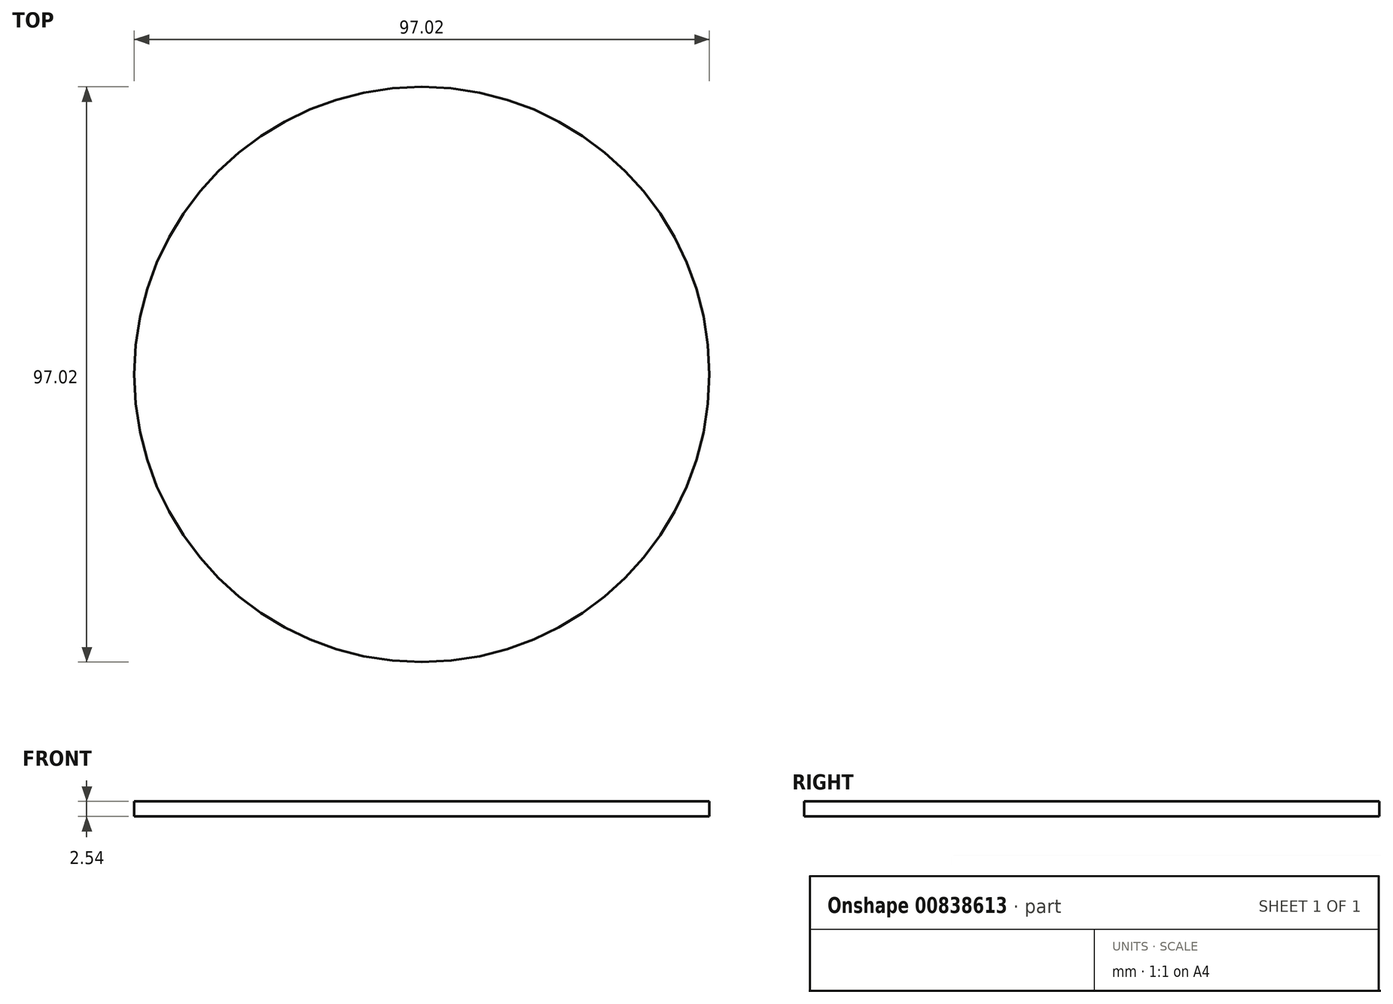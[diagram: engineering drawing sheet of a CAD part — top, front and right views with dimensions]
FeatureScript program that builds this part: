
annotation { "Feature Type Name" : "Feature", "Feature Type Description" : "" }
export const myFeature = defineFeature(function(context is Context, id is Id, definition is map)
    precondition{}
    {
        {
            var Q0;
            Q0=qCreatedBy(makeId("Top.planeOp"),FACE);
            var sketch = newSketch(context, id + "F0", { "sketchPlane" : qUnion([Q0])});
            skCircle(sketch, "E0", {"center": v(0, 0) * mm, "radius": 48.51 * mm});
            skSolve(sketch);
        }
        {
            var Q0;
            Q0=makeQuery(id+"F0.imprint","IMPRINT",FACE,{"disambiguationData":[TD([[makeQuery(id+"F0.imprint","IMPRINT",EDGE,{"derivedFrom":sQuery(id+"F0.wireOp",EDGE,"E0")}),1.0]])]});
            extrude(context, id + "F1", {"entities" : qUnion([Q0]), "depth" : 2.54 * mm, "offsetDistance" : 25.4 * mm});
        }
    });
